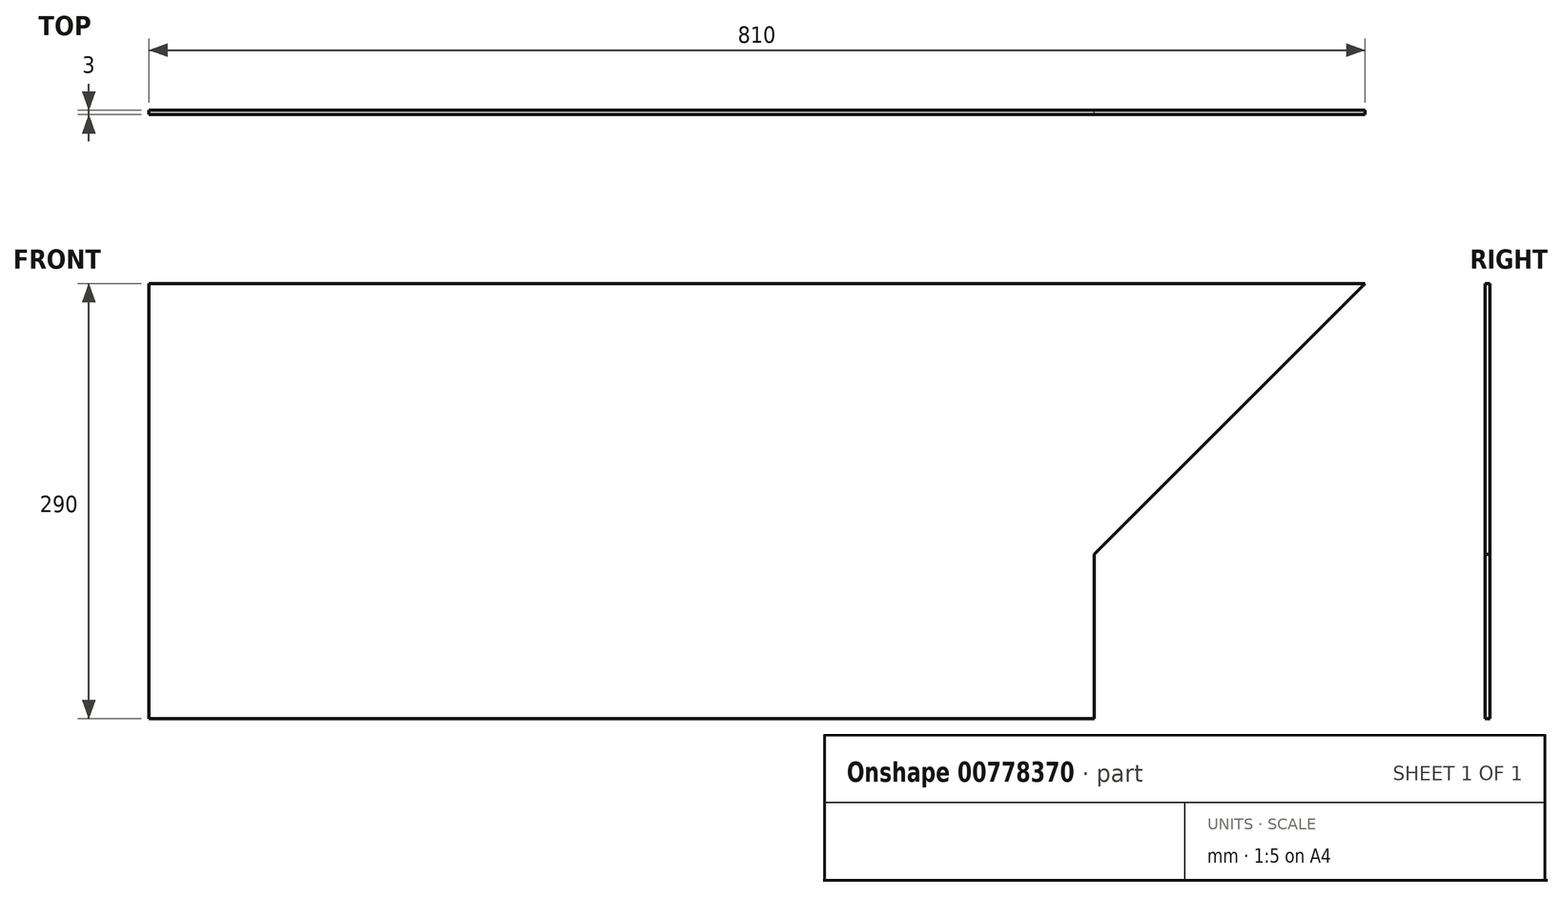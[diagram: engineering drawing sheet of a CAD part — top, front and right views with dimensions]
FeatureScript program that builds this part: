
annotation { "Feature Type Name" : "Feature", "Feature Type Description" : "" }
export const myFeature = defineFeature(function(context is Context, id is Id, definition is map)
    precondition{}
    {
        {
            var Q0;
            Q0=qCreatedBy(makeId("Front.planeOp"),FACE);
            var sketch = newSketch(context, id + "F0", { "sketchPlane" : qUnion([Q0])});
            skLineSegment(sketch, "E0.bottom", {"start": v(0, 0) * mm, "end": v(810, 0) * mm});
            skLineSegment(sketch, "E0.top", {"start": v(0, 290) * mm, "end": v(810, 290) * mm});
            skLineSegment(sketch, "E0.left", {"start": v(0, 0) * mm, "end": v(0, 290) * mm});
            skLineSegment(sketch, "E0.right", {"start": v(810, 0) * mm, "end": v(810, 290) * mm});
            skLineSegment(sketch, "E1", {"start": v(810, 290) * mm, "end": v(629.69, 109.69) * mm});
            skLineSegment(sketch, "E2", {"start": v(629.69, 109.69) * mm, "end": v(629.69, 0) * mm});
            skSolve(sketch);
        }
        {
            var Q0;
            Q0=makeQuery(id+"F0.imprint","IMPRINT",FACE,{"disambiguationData":[TD([[makeQuery(id+"F0.imprint","IMPRINT",EDGE,{"derivedFrom":sQuery(id+"F0.wireOp",EDGE,"E0.top")}),-1.0]])]});
            extrude(context, id + "F1", {"entities" : qUnion([Q0]), "depth" : 3 * mm, "offsetDistance" : 25 * mm});
        }
    });
